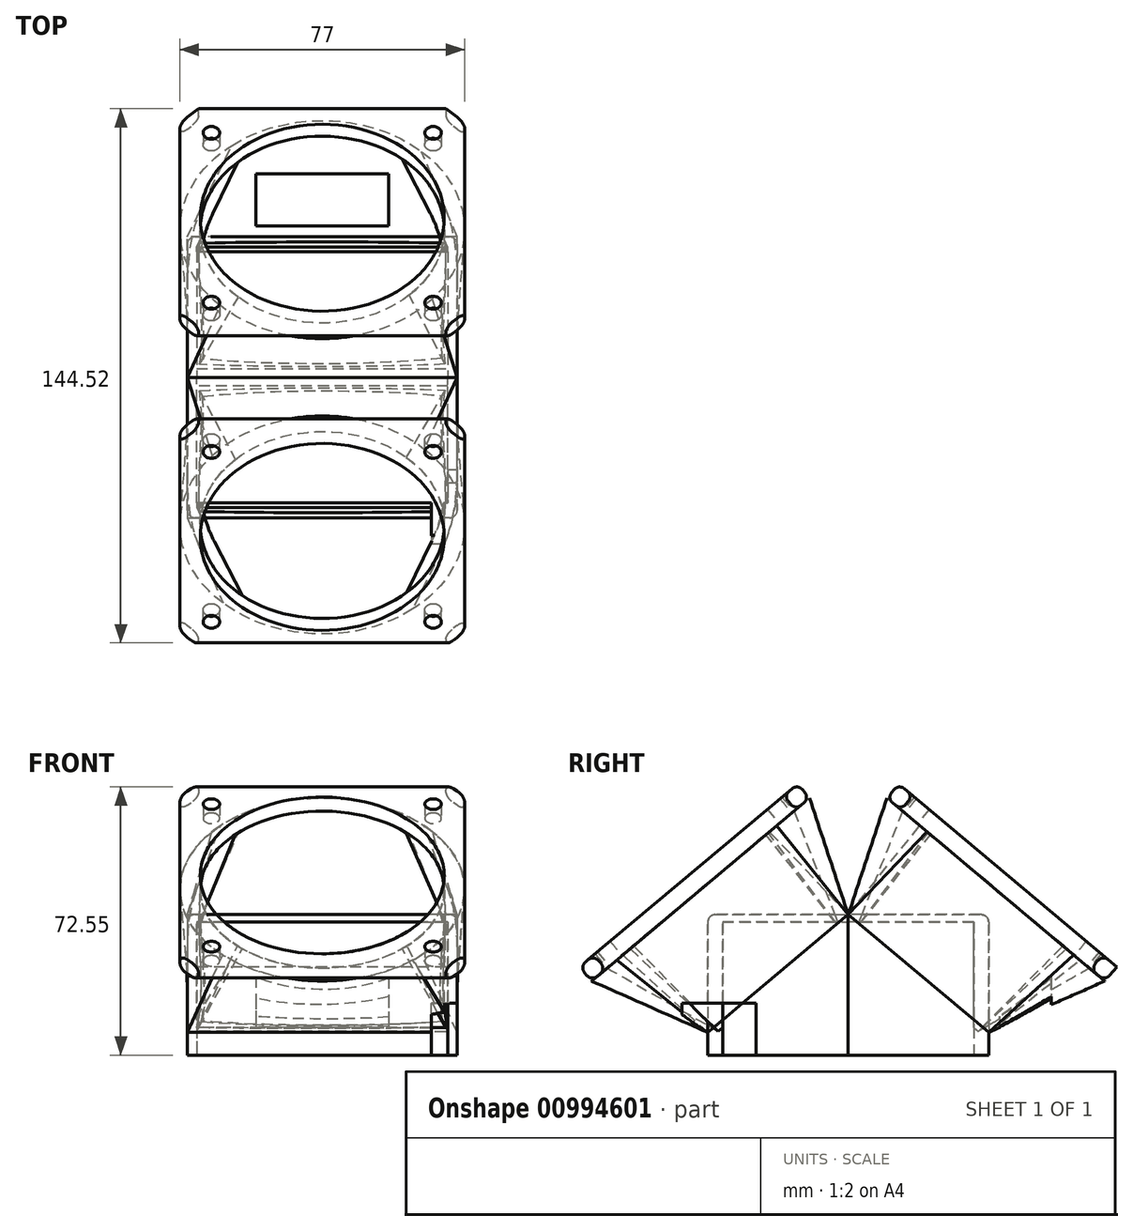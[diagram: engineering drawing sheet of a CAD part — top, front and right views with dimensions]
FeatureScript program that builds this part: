
annotation { "Feature Type Name" : "Feature", "Feature Type Description" : "" }
export const myFeature = defineFeature(function(context is Context, id is Id, definition is map)
    precondition{}
    {
        {
            var Q0;
            Q0=qCreatedBy(makeId("Front.planeOp"),FACE);
            var sketch = newSketch(context, id + "F0", { "sketchPlane" : qUnion([Q0])});
            skLineSegment(sketch, "E0.bottom", {"start": v(-34, 18) * mm, "end": v(34, 18) * mm});
            skLineSegment(sketch, "E0.top", {"start": v(-34, -18) * mm, "end": v(34, -18) * mm});
            skLineSegment(sketch, "E0.left", {"start": v(-34, 18) * mm, "end": v(-34, -18) * mm});
            skLineSegment(sketch, "E0.right", {"start": v(34, 18) * mm, "end": v(34, -18) * mm});
            skPoint(sketch, "E0.middle", {"position": v(0, 0) * mm});
            skSolve(sketch);
        }
        {
            var Q0;
            Q0=makeQuery(id+"F0.imprint","IMPRINT",FACE,{"disambiguationData":[TD([[makeQuery(id+"F0.imprint","IMPRINT",EDGE,{"derivedFrom":sQuery(id+"F0.wireOp",EDGE,"E0.bottom")}),-1.0]])]});
            extrude(context, id + "F1", {"entities" : qUnion([Q0]), "depth" : 34 * mm, "offsetDistance" : 25 * mm});
        }
        {
            var Q0;
            Q0=makeQuery(id+"F0.imprint","IMPRINT",FACE,{"disambiguationData":[TD([[makeQuery(id+"F0.imprint","IMPRINT",EDGE,{"derivedFrom":sQuery(id+"F0.wireOp",EDGE,"E0.bottom")}),-1.0]])]});
            var sketch = newSketch(context, id + "F2", { "sketchPlane" : qUnion([Q0])});
            skLineSegment(sketch, "E1", {"start": v(0, 18) * mm, "end": v(0, -18) * mm, "construction": true});
            skSolve(sketch);
        }
        {
            var Q0;
            Q0=sQuery(id+"F0.wireOp",EDGE,"E0.top");
            cPlane(context, id + "F3", {"entities" : qUnion([Q0]), "cplaneType" : CPlaneType.LINE_ANGLE, "offset" : 25 * mm, "angle" : 50 * degree, "oppositeDirection" : true, "width" : 150 * mm, "height" : 150 * mm});
        }
        {
            var Q0;
            Q0=sQuery(id+"F0.wireOp",EDGE,"E0.bottom");
            var Q1;
            Q1=qBodyType(qCreatedBy(id+"F5",EDGE),BodyType.WIRE);
            cPlane(context, id + "F4", {"entities" : qUnion([Q0, Q1]), "cplaneType" : CPlaneType.LINE_ANGLE, "offset" : 25 * mm, "angle" : 50 * degree, "oppositeDirection" : true, "width" : 150 * mm, "height" : 150 * mm});
        }
        {
            var Q0;
            Q0=qCreatedBy(id+"F4.planeOp",FACE);
            var sketch = newSketch(context, id + "F5", { "sketchPlane" : qUnion([Q0])});
            skLineSegment(sketch, "E2.bottom", {"start": v(34, -8.77) * mm, "end": v(-34, -8.77) * mm});
            skLineSegment(sketch, "E2.top", {"start": v(34, 34.4) * mm, "end": v(-34, 34.4) * mm});
            skLineSegment(sketch, "E2.left", {"start": v(34, -8.77) * mm, "end": v(34, 34.4) * mm});
            skLineSegment(sketch, "E2.right", {"start": v(-34, -8.77) * mm, "end": v(-34, 34.4) * mm});
            skSolve(sketch);
        }
        {
            var Q0;
            Q0=qCreatedBy(id+"F3.planeOp",FACE);
            cPlane(context, id + "F6", {"entities" : qUnion([Q0]), "cplaneType" : CPlaneType.OFFSET, "offset" : 60 * mm, "oppositeDirection" : true, "width" : 150 * mm, "height" : 150 * mm});
        }
        {
            var Q0;
            Q0=qCreatedBy(id+"F6.planeOp",FACE);
            var sketch = newSketch(context, id + "F7", { "sketchPlane" : qUnion([Q0])});
            skArc(sketch, "E3", {"start": v(22.98, 37.08) * mm, "mid": v(0.9, 46.38) * mm, "end": v(-21.64, 38.3) * mm});
            skArc(sketch, "E4", {"start": v(-21.64, 38.3) * mm, "mid": v(-32.97, 14.69) * mm, "end": v(-23.53, -9.74) * mm});
            skArc(sketch, "E5", {"start": v(-23.53, -9.74) * mm, "mid": v(-0.57, -19.6) * mm, "end": v(22.72, -10.54) * mm});
            skArc(sketch, "E6", {"start": v(22.72, -10.54) * mm, "mid": v(33, 13.22) * mm, "end": v(22.98, 37.08) * mm});
            skSolve(sketch);
        }
        {
            var Q0;
            Q0=qSketchRegion(id+"F5",true);
            var Q1;
            Q1=makeQuery(id+"F7.imprint","IMPRINT",FACE,{"disambiguationData":[TD([[makeQuery(id+"F7.imprint","IMPRINT",EDGE,{"derivedFrom":sQuery(id+"F7.wireOp",EDGE,"E3")}),1.0]])]});
            loft(context, id + "F8", {"sheetProfilesArray" : [{ "sheetProfileEntities" : qUnion([Q0]) }, { "sheetProfileEntities" : qUnion([Q1]) }]});
        }
        {
            var Q0;
            Q0=makeQuery(id+"F2.imprint","IMPRINT",FACE,{"disambiguationData":[TD([[makeQuery(id+"F2.imprint","IMPRINT",EDGE,{"derivedFrom":makeQuery(id+"F0.imprint","IMPRINT",EDGE,{"derivedFrom":sQuery(id+"F0.wireOp",EDGE,"E0.bottom")})}),-1.0]])]});
            var sketch = newSketch(context, id + "F9", { "sketchPlane" : qUnion([Q0])});
            skLineSegment(sketch, "E7.bottom", {"start": v(36.5, 20) * mm, "end": v(-36.5, 20) * mm});
            skLineSegment(sketch, "E7.top", {"start": v(36.5, -18) * mm, "end": v(-36.5, -18) * mm});
            skLineSegment(sketch, "E7.left", {"start": v(36.5, 20) * mm, "end": v(36.5, -18) * mm});
            skLineSegment(sketch, "E7.right", {"start": v(-36.5, 20) * mm, "end": v(-36.5, -18) * mm});
            skPoint(sketch, "E7.middle", {"position": v(0, 0) * mm});
            skSolve(sketch);
        }
        {
            var Q0;
            Q0=qSketchRegion(id+"F9",true);
            extrude(context, id + "F10", {"entities" : qUnion([Q0]), "depth" : 38 * mm, "offsetDistance" : 25 * mm});
        }
        {
            var Q0;
            Q0=sQuery(id+"F9.wireOp",EDGE,"E7.bottom");
            cPlane(context, id + "F11", {"entities" : qUnion([Q0]), "cplaneType" : CPlaneType.LINE_ANGLE, "offset" : 25 * mm, "angle" : 50 * degree, "width" : 150 * mm, "height" : 150 * mm});
        }
        {
            var Q0;
            Q0=qCreatedBy(id+"F11.planeOp",FACE);
            var sketch = newSketch(context, id + "F12", { "sketchPlane" : qUnion([Q0])});
            skLineSegment(sketch, "E8.bottom", {"start": v(-36.5, 12.86) * mm, "end": v(36.5, 12.86) * mm});
            skLineSegment(sketch, "E8.top", {"start": v(-36.5, -36.75) * mm, "end": v(36.5, -36.75) * mm});
            skLineSegment(sketch, "E8.left", {"start": v(-36.5, 12.86) * mm, "end": v(-36.5, -36.75) * mm});
            skLineSegment(sketch, "E8.right", {"start": v(36.5, 12.86) * mm, "end": v(36.5, -36.75) * mm});
            skSolve(sketch);
        }
        {
            var Q0;
            Q0=qCreatedBy(id+"F6.planeOp",FACE);
            var sketch = newSketch(context, id + "F13", { "sketchPlane" : qUnion([Q0])});
            skArc(sketch, "E9", {"start": v(-29.82, -10.96) * mm, "mid": v(-1.7, -25.07) * mm, "end": v(27.55, -13.5) * mm});
            skArc(sketch, "E10", {"start": v(27.55, -13.5) * mm, "mid": v(38.44, 15.46) * mm, "end": v(24.51, 43.08) * mm});
            skArc(sketch, "E11", {"start": v(24.51, 43.08) * mm, "mid": v(-1.62, 51.86) * mm, "end": v(-26.92, 40.91) * mm});
            skArc(sketch, "E12", {"start": v(-26.92, 40.91) * mm, "mid": v(-38.44, 15.54) * mm, "end": v(-29.82, -10.96) * mm});
            skSolve(sketch);
        }
        {
            var Q0;
            Q0=qCreatedBy(id+"F6.planeOp",FACE);
            var sketch = newSketch(context, id + "F14", { "sketchPlane" : qUnion([Q0])});
            skLineSegment(sketch, "E13.bottom", {"start": v(-38.5, -25.1) * mm, "end": v(38.5, -25.1) * mm});
            skLineSegment(sketch, "E13.top", {"start": v(-38.5, 51.9) * mm, "end": v(38.5, 51.9) * mm});
            skLineSegment(sketch, "E13.left", {"start": v(-38.5, -25.1) * mm, "end": v(-38.5, 51.9) * mm});
            skLineSegment(sketch, "E13.right", {"start": v(38.5, -25.1) * mm, "end": v(38.5, 51.9) * mm});
            skPoint(sketch, "E13.middle", {"position": v(0, 13.4) * mm});
            skSolve(sketch);
        }
        {
            var Q0;
            Q0=qCreatedBy(id+"F6.planeOp",FACE);
            var sketch = newSketch(context, id + "F15", { "sketchPlane" : qUnion([Q0])});
            skLineSegment(sketch, "E14.bottom", {"start": v(-30, -16.6) * mm, "end": v(30, -16.6) * mm, "construction": true});
            skLineSegment(sketch, "E14.top", {"start": v(-30, 43.4) * mm, "end": v(30, 43.4) * mm, "construction": true});
            skLineSegment(sketch, "E14.left", {"start": v(-30, -16.6) * mm, "end": v(-30, 43.4) * mm, "construction": true});
            skLineSegment(sketch, "E14.right", {"start": v(30, -16.6) * mm, "end": v(30, 43.4) * mm, "construction": true});
            skPoint(sketch, "E14.middle", {"position": v(0, 13.4) * mm});
            skSolve(sketch);
        }
        {
            var Q0;
            Q0=qCreatedBy(id+"F6.planeOp",FACE);
            var sketch = newSketch(context, id + "F16", { "sketchPlane" : qUnion([Q0])});
            skCircle(sketch, "E15", {"center": v(30, -16.6) * mm, "radius": 2.25 * mm});
            skCircle(sketch, "E16", {"center": v(-30, -16.6) * mm, "radius": 2.25 * mm});
            skCircle(sketch, "E17", {"center": v(-30, 43.4) * mm, "radius": 2.25 * mm});
            skCircle(sketch, "E18", {"center": v(30, 43.4) * mm, "radius": 2.25 * mm});
            skSolve(sketch);
        }
        {
            var Q0;
            Q0=makeQuery(id+"F8.opLoft","CAP_FACE",FACE,{"disambiguationData":[OSD([makeQuery(id+"F7.imprint","IMPRINT",FACE,{"disambiguationData":[TD([[makeQuery(id+"F7.imprint","IMPRINT",EDGE,{"derivedFrom":sQuery(id+"F7.wireOp",EDGE,"E3")}),1.0]])]})])],"isStart":true});
            var Q1;
            Q1=makeQuery(id+"F16.imprint","IMPRINT",FACE,{"disambiguationData":[TD([[makeQuery(id+"F16.imprint","IMPRINT",EDGE,{"derivedFrom":sQuery(id+"F16.wireOp",EDGE,"E18")}),1.0]])]});
            var Q2;
            Q2=makeQuery(id+"F16.imprint","IMPRINT",FACE,{"disambiguationData":[TD([[makeQuery(id+"F16.imprint","IMPRINT",EDGE,{"derivedFrom":sQuery(id+"F16.wireOp",EDGE,"E17")}),1.0]])]});
            var Q3;
            Q3=makeQuery(id+"F16.imprint","IMPRINT",FACE,{"disambiguationData":[TD([[makeQuery(id+"F16.imprint","IMPRINT",EDGE,{"derivedFrom":sQuery(id+"F16.wireOp",EDGE,"E16")}),1.0]])]});
            var Q4;
            Q4=makeQuery(id+"F16.imprint","IMPRINT",FACE,{"disambiguationData":[TD([[makeQuery(id+"F16.imprint","IMPRINT",EDGE,{"derivedFrom":sQuery(id+"F16.wireOp",EDGE,"E15")}),1.0]])]});
            extrude(context, id + "F17", {"entities" : qUnion([Q0, Q1, Q2, Q3, Q4]), "depth" : 5 * mm, "offsetDistance" : 25 * mm});
        }
        {
            var Q0;
            Q0=makeQuery(id+"F12.imprint","IMPRINT",FACE,{"disambiguationData":[TD([[makeQuery(id+"F12.imprint","IMPRINT",EDGE,{"derivedFrom":sQuery(id+"F12.wireOp",EDGE,"E8.bottom")}),-1.0]])]});
            var Q1;
            Q1=qSketchRegion(id+"F13",true);
            loft(context, id + "F18", {"sheetProfilesArray" : [{ "sheetProfileEntities" : qUnion([Q0]) }, { "sheetProfileEntities" : qUnion([Q1]) }]});
        }
        {
            var Q0;
            Q0=makeQuery(id+"F14.imprint","IMPRINT",FACE,{"disambiguationData":[TD([[makeQuery(id+"F14.imprint","IMPRINT",EDGE,{"derivedFrom":sQuery(id+"F14.wireOp",EDGE,"E13.bottom")}),1.0]])]});
            extrude(context, id + "F19", {"entities" : qUnion([Q0]), "oppositeDirection" : true, "depth" : 5 * mm, "offsetDistance" : 25 * mm});
        }
        {
            var Q0;
            Q0=makeQuery(id+"F17.opExtrude","SWEPT_BODY",BODY,{"disambiguationData":[OSD([sQuery(id+"F16.wireOp",EDGE,"E18")])]});
            var Q1;
            Q1=makeQuery(id+"F17.opExtrude","SWEPT_BODY",BODY,{"disambiguationData":[OSD([sQuery(id+"F16.wireOp",EDGE,"E17")])]});
            var Q2;
            Q2=makeQuery(id+"F17.opExtrude","SWEPT_BODY",BODY,{"disambiguationData":[OSD([sQuery(id+"F16.wireOp",EDGE,"E16")])]});
            var Q3;
            Q3=makeQuery(id+"F17.opExtrude","SWEPT_BODY",BODY,{"disambiguationData":[OSD([sQuery(id+"F16.wireOp",EDGE,"E15")])]});
            var Q4;
            Q4=makeQuery(id+"F17.opExtrude","SWEPT_BODY",BODY,{"disambiguationData":[OSD([makeQuery(id+"F7.imprint","IMPRINT",FACE,{"disambiguationData":[TD([[makeQuery(id+"F7.imprint","IMPRINT",EDGE,{"derivedFrom":sQuery(id+"F7.wireOp",EDGE,"E3")}),1.0]])]})])]});
            var Q5;
            Q5=makeQuery(id+"F8.opLoft","SWEPT_BODY",BODY,{"disambiguationData":[OSD([makeQuery(id+"F5.imprint","IMPRINT",FACE,{"disambiguationData":[TD([[makeQuery(id+"F5.imprint","IMPRINT",EDGE,{"derivedFrom":sQuery(id+"F5.wireOp",EDGE,"sHmJ6Bm4-Lffu-TfJG-ELbj-xKBSEGzgKOYK.bottom")}),-1.0]])]}),makeQuery(id+"F7.imprint","IMPRINT",FACE,{"disambiguationData":[TD([[makeQuery(id+"F7.imprint","IMPRINT",EDGE,{"derivedFrom":sQuery(id+"F7.wireOp",EDGE,"E3")}),1.0]])]})])]});
            var Q6;
            Q6=makeQuery(id+"F1.opExtrude","SWEPT_BODY",BODY,{"disambiguationData":[OSD([sQuery(id+"F0.wireOp",EDGE,"E0.bottom"),sQuery(id+"F0.wireOp",EDGE,"E0.top"),sQuery(id+"F0.wireOp",EDGE,"E0.left"),sQuery(id+"F0.wireOp",EDGE,"E0.right")])]});
            var Q7;
            Q7=makeQuery(id+"F10.opExtrude","SWEPT_BODY",BODY,{"disambiguationData":[OSD([sQuery(id+"F9.wireOp",EDGE,"E7.bottom"),sQuery(id+"F9.wireOp",EDGE,"E7.top"),sQuery(id+"F9.wireOp",EDGE,"E7.left"),sQuery(id+"F9.wireOp",EDGE,"E7.right")])]});
            var Q8;
            Q8=makeQuery(id+"F18.opLoft","SWEPT_BODY",BODY,{"disambiguationData":[OSD([makeQuery(id+"F12.imprint","IMPRINT",FACE,{"disambiguationData":[TD([[makeQuery(id+"F12.imprint","IMPRINT",EDGE,{"derivedFrom":sQuery(id+"F12.wireOp",EDGE,"E8.bottom")}),-1.0]])]}),makeQuery(id+"F13.imprint","IMPRINT",FACE,{"disambiguationData":[TD([[makeQuery(id+"F13.imprint","IMPRINT",EDGE,{"derivedFrom":sQuery(id+"F13.wireOp",EDGE,"q23MTACi-eoCC-Vc5T-UU1i-hVDggLDGJppy")}),1.0]])]})])]});
            var Q9;
            Q9=makeQuery(id+"F19.opExtrude","SWEPT_BODY",BODY,{"disambiguationData":[OSD([sQuery(id+"F14.wireOp",EDGE,"E13.bottom"),sQuery(id+"F14.wireOp",EDGE,"E13.top"),sQuery(id+"F14.wireOp",EDGE,"E13.left"),sQuery(id+"F14.wireOp",EDGE,"E13.right")])]});
            booleanBodies(context, id + "F20", {"operationType" : BooleanOperationType.SUBTRACTION, "tools" : qUnion([Q0, Q1, Q2, Q3, Q4, Q5, Q6]), "targets" : qUnion([Q7, Q8, Q9])});
        }
        {
            var Q0;
            Q0=makeQuery(id+"F10.opExtrude","SWEPT_BODY",BODY,{"disambiguationData":[OSD([sQuery(id+"F9.wireOp",EDGE,"E7.bottom"),sQuery(id+"F9.wireOp",EDGE,"E7.top"),sQuery(id+"F9.wireOp",EDGE,"E7.left"),sQuery(id+"F9.wireOp",EDGE,"E7.right")])]});
            var Q1;
            Q1=sQuery(id+"F2.wireOp",EDGE,"E1");
            transform(context, id + "F21", {"entities" : qUnion([Q0]), "transformType" : TransformType.ROTATION, "transformAxis" : qUnion([Q1]), "angle" : 180 * degree, "makeCopy" : true});
        }
        {
            var Q0;
            Q0=makeQuery(id+"F18.opLoft","SWEPT_BODY",BODY,{"disambiguationData":[OSD([makeQuery(id+"F12.imprint","IMPRINT",FACE,{"disambiguationData":[TD([[makeQuery(id+"F12.imprint","IMPRINT",EDGE,{"derivedFrom":sQuery(id+"F12.wireOp",EDGE,"E8.bottom")}),-1.0]])]}),makeQuery(id+"F13.imprint","IMPRINT",FACE,{"disambiguationData":[TD([[makeQuery(id+"F13.imprint","IMPRINT",EDGE,{"derivedFrom":sQuery(id+"F13.wireOp",EDGE,"q23MTACi-eoCC-Vc5T-UU1i-hVDggLDGJppy")}),1.0]])]})])]});
            var Q1;
            Q1=sQuery(id+"F2.wireOp",EDGE,"E1");
            transform(context, id + "F22", {"entities" : qUnion([Q0]), "transformType" : TransformType.ROTATION, "transformAxis" : qUnion([Q1]), "angle" : 180 * degree, "makeCopy" : true});
        }
        {
            var Q0;
            Q0=makeQuery(id+"F19.opExtrude","SWEPT_BODY",BODY,{"disambiguationData":[OSD([sQuery(id+"F14.wireOp",EDGE,"E13.bottom"),sQuery(id+"F14.wireOp",EDGE,"E13.top"),sQuery(id+"F14.wireOp",EDGE,"E13.left"),sQuery(id+"F14.wireOp",EDGE,"E13.right")])]});
            var Q1;
            Q1=sQuery(id+"F2.wireOp",EDGE,"E1");
            transform(context, id + "F23", {"entities" : qUnion([Q0]), "transformType" : TransformType.ROTATION, "transformAxis" : qUnion([Q1]), "angle" : 180 * degree, "makeCopy" : true});
        }
        {
            var Q0;
            Q0=makeQuery(id+"F19.opExtrude","SWEPT_EDGE",EDGE,{"disambiguationData":[OSD([sQuery(id+"F14.wireOp",EDGE,"E13.top"),sQuery(id+"F14.wireOp",EDGE,"E13.right")])]});
            var Q1;
            Q1=makeQuery(id+"F19.opExtrude","SWEPT_EDGE",EDGE,{"disambiguationData":[OSD([sQuery(id+"F14.wireOp",EDGE,"E13.top"),sQuery(id+"F14.wireOp",EDGE,"E13.left")])]});
            var Q2;
            Q2=makeQuery(id+"F19.opExtrude","SWEPT_EDGE",EDGE,{"disambiguationData":[OSD([sQuery(id+"F14.wireOp",EDGE,"E13.bottom"),sQuery(id+"F14.wireOp",EDGE,"E13.right")])]});
            var Q3;
            Q3=makeQuery(id+"F19.opExtrude","SWEPT_EDGE",EDGE,{"disambiguationData":[OSD([sQuery(id+"F14.wireOp",EDGE,"E13.bottom"),sQuery(id+"F14.wireOp",EDGE,"E13.left")])]});
            var Q4;
            Q4=makeQuery(id+"F23.opPattern","COPY",EDGE,{"derivedFrom":makeQuery(id+"F19.opExtrude","SWEPT_EDGE",EDGE,{"disambiguationData":[OSD([sQuery(id+"F14.wireOp",EDGE,"E13.bottom"),sQuery(id+"F14.wireOp",EDGE,"E13.right")])]}),"instanceName":"1"});
            var Q5;
            Q5=makeQuery(id+"F23.opPattern","COPY",EDGE,{"derivedFrom":makeQuery(id+"F19.opExtrude","SWEPT_EDGE",EDGE,{"disambiguationData":[OSD([sQuery(id+"F14.wireOp",EDGE,"E13.bottom"),sQuery(id+"F14.wireOp",EDGE,"E13.left")])]}),"instanceName":"1"});
            var Q6;
            Q6=makeQuery(id+"F23.opPattern","COPY",EDGE,{"derivedFrom":makeQuery(id+"F19.opExtrude","SWEPT_EDGE",EDGE,{"disambiguationData":[OSD([sQuery(id+"F14.wireOp",EDGE,"E13.top"),sQuery(id+"F14.wireOp",EDGE,"E13.left")])]}),"instanceName":"1"});
            var Q7;
            Q7=makeQuery(id+"F23.opPattern","COPY",EDGE,{"derivedFrom":makeQuery(id+"F19.opExtrude","SWEPT_EDGE",EDGE,{"disambiguationData":[OSD([sQuery(id+"F14.wireOp",EDGE,"E13.top"),sQuery(id+"F14.wireOp",EDGE,"E13.right")])]}),"instanceName":"1"});
            chamfer(context, id + "F24", {"entities" : qUnion([Q0, Q1, Q2, Q3, Q4, Q5, Q6, Q7]), "width" : 5 * mm, "tangentPropagation" : true});
        }
        {
            var Q0;
            Q0=makeQuery(id+"F19.opExtrude","CAP_EDGE",EDGE,{"disambiguationData":[OSD([sQuery(id+"F14.wireOp",EDGE,"E13.left")])],"isStart":false});
            var Q1;
            Q1=makeQuery(id+"F19.opExtrude","CAP_EDGE",EDGE,{"disambiguationData":[OSD([sQuery(id+"F14.wireOp",EDGE,"E13.top")])],"isStart":false});
            var Q2;
            Q2=makeQuery(id+"F19.opExtrude","CAP_EDGE",EDGE,{"disambiguationData":[OSD([sQuery(id+"F14.wireOp",EDGE,"E13.right")])],"isStart":false});
            var Q3;
            Q3=makeQuery(id+"F19.opExtrude","CAP_EDGE",EDGE,{"disambiguationData":[OSD([sQuery(id+"F14.wireOp",EDGE,"E13.bottom")])],"isStart":false});
            var Q4;
            Q4=makeQuery(id+"F19.opExtrude","CAP_EDGE",EDGE,{"disambiguationData":[OSD([sQuery(id+"F14.wireOp",EDGE,"E13.left")])],"isStart":true});
            var Q5;
            Q5=makeQuery(id+"F19.opExtrude","CAP_EDGE",EDGE,{"disambiguationData":[OSD([sQuery(id+"F14.wireOp",EDGE,"E13.bottom")])],"isStart":true});
            var Q6;
            Q6=makeQuery(id+"F19.opExtrude","CAP_EDGE",EDGE,{"disambiguationData":[OSD([sQuery(id+"F14.wireOp",EDGE,"E13.right")])],"isStart":true});
            var Q7;
            Q7=makeQuery(id+"F19.opExtrude","CAP_EDGE",EDGE,{"disambiguationData":[OSD([sQuery(id+"F14.wireOp",EDGE,"E13.top")])],"isStart":true});
            var Q8;
            Q8=makeQuery(id+"F10.opExtrude","CAP_EDGE",EDGE,{"disambiguationData":[OSD([sQuery(id+"F9.wireOp",EDGE,"E7.right")])],"isStart":false});
            var Q9;
            {var subQ0=sQuery(id+"F9.wireOp",EDGE,"E7.bottom");var subQ1=sQuery(id+"F9.wireOp",EDGE,"E7.right");Q9=makeQuery(id+"F20.opBoolean","SPLIT",EDGE,{"disambiguationData":[TD([makeQuery(id+"F10.opExtrude","SWEPT_FACE",FACE,{"disambiguationData":[OSD([subQ1])]})])],"derivedFrom":makeQuery(id+"F10.opExtrude","CAP_EDGE",EDGE,{"disambiguationData":[OSD([subQ0])],"isStart":false})});}
            var Q10;
            Q10=makeQuery(id+"F10.opExtrude","SWEPT_EDGE",EDGE,{"disambiguationData":[OSD([sQuery(id+"F9.wireOp",EDGE,"E7.bottom"),sQuery(id+"F9.wireOp",EDGE,"E7.right")])]});
            var Q11;
            Q11=makeQuery(id+"F10.opExtrude","CAP_EDGE",EDGE,{"disambiguationData":[OSD([sQuery(id+"F9.wireOp",EDGE,"E7.left")])],"isStart":false});
            var Q12;
            Q12=makeQuery(id+"F10.opExtrude","SWEPT_EDGE",EDGE,{"disambiguationData":[OSD([sQuery(id+"F9.wireOp",EDGE,"E7.bottom"),sQuery(id+"F9.wireOp",EDGE,"E7.left")])]});
            var Q13;
            {var subQ0=sQuery(id+"F9.wireOp",EDGE,"E7.bottom");var subQ1=sQuery(id+"F9.wireOp",EDGE,"E7.left");Q13=makeQuery(id+"F20.opBoolean","SPLIT",EDGE,{"disambiguationData":[TD([makeQuery(id+"F10.opExtrude","SWEPT_FACE",FACE,{"disambiguationData":[OSD([subQ1])]})])],"derivedFrom":makeQuery(id+"F10.opExtrude","CAP_EDGE",EDGE,{"disambiguationData":[OSD([subQ0])],"isStart":false})});}
            var Q14;
            Q14=makeQuery(id+"F21.opPattern","COPY",EDGE,{"derivedFrom":makeQuery(id+"F10.opExtrude","SWEPT_EDGE",EDGE,{"disambiguationData":[OSD([sQuery(id+"F9.wireOp",EDGE,"E7.bottom"),sQuery(id+"F9.wireOp",EDGE,"E7.right")])]}),"instanceName":"1"});
            var Q15;
            {var subQ0=sQuery(id+"F9.wireOp",EDGE,"E7.bottom");var subQ1=sQuery(id+"F9.wireOp",EDGE,"E7.right");Q15=makeQuery(id+"F21.opPattern","COPY",EDGE,{"derivedFrom":makeQuery(id+"F20.opBoolean","SPLIT",EDGE,{"disambiguationData":[TD([makeQuery(id+"F10.opExtrude","SWEPT_FACE",FACE,{"disambiguationData":[OSD([subQ1])]})])],"derivedFrom":makeQuery(id+"F10.opExtrude","CAP_EDGE",EDGE,{"disambiguationData":[OSD([subQ0])],"isStart":false})}),"instanceName":"1"});}
            var Q16;
            Q16=makeQuery(id+"F21.opPattern","COPY",EDGE,{"derivedFrom":makeQuery(id+"F10.opExtrude","CAP_EDGE",EDGE,{"disambiguationData":[OSD([sQuery(id+"F9.wireOp",EDGE,"E7.right")])],"isStart":false}),"instanceName":"1"});
            var Q17;
            Q17=makeQuery(id+"F23.opPattern","COPY",EDGE,{"derivedFrom":makeQuery(id+"F19.opExtrude","CAP_EDGE",EDGE,{"disambiguationData":[OSD([sQuery(id+"F14.wireOp",EDGE,"E13.right")])],"isStart":false}),"instanceName":"1"});
            var Q18;
            Q18=makeQuery(id+"F23.opPattern","COPY",EDGE,{"derivedFrom":makeQuery(id+"F19.opExtrude","CAP_EDGE",EDGE,{"disambiguationData":[OSD([sQuery(id+"F14.wireOp",EDGE,"E13.right")])],"isStart":true}),"instanceName":"1"});
            var Q19;
            Q19=makeQuery(id+"F23.opPattern","COPY",EDGE,{"derivedFrom":makeQuery(id+"F19.opExtrude","CAP_EDGE",EDGE,{"disambiguationData":[OSD([sQuery(id+"F14.wireOp",EDGE,"E13.top")])],"isStart":true}),"instanceName":"1"});
            var Q20;
            Q20=makeQuery(id+"F23.opPattern","COPY",EDGE,{"derivedFrom":makeQuery(id+"F19.opExtrude","CAP_EDGE",EDGE,{"disambiguationData":[OSD([sQuery(id+"F14.wireOp",EDGE,"E13.bottom")])],"isStart":true}),"instanceName":"1"});
            var Q21;
            Q21=makeQuery(id+"F23.opPattern","COPY",EDGE,{"derivedFrom":makeQuery(id+"F19.opExtrude","CAP_EDGE",EDGE,{"disambiguationData":[OSD([sQuery(id+"F14.wireOp",EDGE,"E13.bottom")])],"isStart":false}),"instanceName":"1"});
            var Q22;
            Q22=makeQuery(id+"F23.opPattern","COPY",EDGE,{"derivedFrom":makeQuery(id+"F19.opExtrude","CAP_EDGE",EDGE,{"disambiguationData":[OSD([sQuery(id+"F14.wireOp",EDGE,"E13.left")])],"isStart":false}),"instanceName":"1"});
            var Q23;
            Q23=makeQuery(id+"F23.opPattern","COPY",EDGE,{"derivedFrom":makeQuery(id+"F19.opExtrude","CAP_EDGE",EDGE,{"disambiguationData":[OSD([sQuery(id+"F14.wireOp",EDGE,"E13.left")])],"isStart":true}),"instanceName":"1"});
            var Q24;
            Q24=makeQuery(id+"F21.opPattern","COPY",EDGE,{"derivedFrom":makeQuery(id+"F10.opExtrude","CAP_EDGE",EDGE,{"disambiguationData":[OSD([sQuery(id+"F9.wireOp",EDGE,"E7.left")])],"isStart":false}),"instanceName":"1"});
            var Q25;
            {var subQ0=sQuery(id+"F9.wireOp",EDGE,"E7.bottom");var subQ1=sQuery(id+"F9.wireOp",EDGE,"E7.left");Q25=makeQuery(id+"F21.opPattern","COPY",EDGE,{"derivedFrom":makeQuery(id+"F20.opBoolean","SPLIT",EDGE,{"disambiguationData":[TD([makeQuery(id+"F10.opExtrude","SWEPT_FACE",FACE,{"disambiguationData":[OSD([subQ1])]})])],"derivedFrom":makeQuery(id+"F10.opExtrude","CAP_EDGE",EDGE,{"disambiguationData":[OSD([subQ0])],"isStart":false})}),"instanceName":"1"});}
            var Q26;
            Q26=makeQuery(id+"F21.opPattern","COPY",EDGE,{"derivedFrom":makeQuery(id+"F10.opExtrude","SWEPT_EDGE",EDGE,{"disambiguationData":[OSD([sQuery(id+"F9.wireOp",EDGE,"E7.bottom"),sQuery(id+"F9.wireOp",EDGE,"E7.left")])]}),"instanceName":"1"});
            fillet(context, id + "F25", {"entities" : qUnion([Q0, Q1, Q2, Q3, Q4, Q5, Q6, Q7, Q8, Q9, Q10, Q11, Q12, Q13, Q14, Q15, Q16, Q17, Q18, Q19, Q20, Q21, Q22, Q23, Q24, Q25, Q26]), "radius" : 2 * mm, "tangentPropagation" : true, "allowEdgeOverflow" : false});
        }
        {
            var Q0;
            Q0=makeQuery(id+"F10.opExtrude","SWEPT_FACE",FACE,{"disambiguationData":[OSD([sQuery(id+"F9.wireOp",EDGE,"E7.left")])]});
            var sketch = newSketch(context, id + "F26", { "sketchPlane" : qUnion([Q0])});
            skLineSegment(sketch, "E19.bottom", {"start": v(-25, -19) * mm, "end": v(-45, -19) * mm});
            skLineSegment(sketch, "E19.top", {"start": v(-25, -4) * mm, "end": v(-45, -4) * mm});
            skLineSegment(sketch, "E19.left", {"start": v(-25, -19) * mm, "end": v(-25, -4) * mm});
            skLineSegment(sketch, "E19.right", {"start": v(-45, -19) * mm, "end": v(-45, -4) * mm});
            skSolve(sketch);
        }
        {
            var Q0;
            Q0=qSketchRegion(id+"F26",true);
            extrude(context, id + "F27", {"entities" : qUnion([Q0]), "oppositeDirection" : true, "depth" : 7 * mm, "offsetDistance" : 25 * mm});
        }
        {
            var Q0;
            Q0=makeQuery(id+"F27.opExtrude","SWEPT_BODY",BODY,{"disambiguationData":[OSD([sQuery(id+"F26.wireOp",EDGE,"E19.bottom"),sQuery(id+"F26.wireOp",EDGE,"E19.top"),sQuery(id+"F26.wireOp",EDGE,"E19.left"),sQuery(id+"F26.wireOp",EDGE,"E19.right")])]});
            var Q1;
            Q1=makeQuery(id+"F10.opExtrude","SWEPT_BODY",BODY,{"disambiguationData":[OSD([sQuery(id+"F9.wireOp",EDGE,"E7.bottom"),sQuery(id+"F9.wireOp",EDGE,"E7.top"),sQuery(id+"F9.wireOp",EDGE,"E7.left"),sQuery(id+"F9.wireOp",EDGE,"E7.right")])]});
            var Q2;
            Q2=makeQuery(id+"F18.opLoft","SWEPT_BODY",BODY,{"disambiguationData":[OSD([makeQuery(id+"F12.imprint","IMPRINT",FACE,{"disambiguationData":[TD([[makeQuery(id+"F12.imprint","IMPRINT",EDGE,{"derivedFrom":sQuery(id+"F12.wireOp",EDGE,"E8.bottom")}),-1.0]])]}),makeQuery(id+"F13.imprint","IMPRINT",FACE,{"disambiguationData":[TD([[makeQuery(id+"F13.imprint","IMPRINT",EDGE,{"derivedFrom":sQuery(id+"F13.wireOp",EDGE,"q23MTACi-eoCC-Vc5T-UU1i-hVDggLDGJppy")}),1.0]])]})])]});
            booleanBodies(context, id + "F28", {"operationType" : BooleanOperationType.SUBTRACTION, "tools" : qUnion([Q0]), "targets" : qUnion([Q1, Q2])});
        }
        {
            var Q0;
            Q0=qCreatedBy(makeId("Top.planeOp"),FACE);
            var sketch = newSketch(context, id + "F29", { "sketchPlane" : qUnion([Q0])});
            skLineSegment(sketch, "E20.bottom", {"start": v(18, 55) * mm, "end": v(-18, 55) * mm});
            skLineSegment(sketch, "E20.top", {"start": v(18, 41) * mm, "end": v(-18, 41) * mm});
            skLineSegment(sketch, "E20.left", {"start": v(18, 55) * mm, "end": v(18, 41) * mm});
            skLineSegment(sketch, "E20.right", {"start": v(-18, 55) * mm, "end": v(-18, 41) * mm});
            skPoint(sketch, "E20.middle", {"position": v(0, 48) * mm});
            skSolve(sketch);
        }
        {
            var Q0;
            Q0 = qSketchRegion(id + "F29", true);
            extrude(context, id + "F30", {"entities" : qUnion([Q0]), "endBound" : BoundingType.SYMMETRIC, "depth" : 25 * mm, "offsetDistance" : 25 * mm});
        }
        {
            var Q0;
            Q0=makeQuery(id+"F30.opExtrude","SWEPT_BODY",BODY,{"disambiguationData":[OSD([sQuery(id+"F29.wireOp",EDGE,"E20.bottom"),sQuery(id+"F29.wireOp",EDGE,"E20.top"),sQuery(id+"F29.wireOp",EDGE,"E20.left"),sQuery(id+"F29.wireOp",EDGE,"E20.right")])]});
            var Q1;
            Q1=makeQuery(id+"F23.opPattern","COPY",BODY,{"derivedFrom":makeQuery(id+"F19.opExtrude","SWEPT_BODY",BODY,{"disambiguationData":[OSD([sQuery(id+"F14.wireOp",EDGE,"E13.bottom"),sQuery(id+"F14.wireOp",EDGE,"E13.top"),sQuery(id+"F14.wireOp",EDGE,"E13.left"),sQuery(id+"F14.wireOp",EDGE,"E13.right")])]}),"instanceName":"1"});
            var Q2;
            Q2=makeQuery(id+"F22.opPattern","COPY",BODY,{"derivedFrom":makeQuery(id+"F18.opLoft","SWEPT_BODY",BODY,{"disambiguationData":[OSD([makeQuery(id+"F12.imprint","IMPRINT",FACE,{"disambiguationData":[TD([[makeQuery(id+"F12.imprint","IMPRINT",EDGE,{"derivedFrom":sQuery(id+"F12.wireOp",EDGE,"E8.bottom")}),-1.0]])]}),makeQuery(id+"F13.imprint","IMPRINT",FACE,{"disambiguationData":[TD([[makeQuery(id+"F13.imprint","IMPRINT",EDGE,{"derivedFrom":sQuery(id+"F13.wireOp",EDGE,"E9")}),1.0]])]})])]}),"instanceName":"1"});
            var Q3;
            Q3=makeQuery(id+"F21.opPattern","COPY",BODY,{"derivedFrom":makeQuery(id+"F10.opExtrude","SWEPT_BODY",BODY,{"disambiguationData":[OSD([sQuery(id+"F9.wireOp",EDGE,"E7.bottom"),sQuery(id+"F9.wireOp",EDGE,"E7.top"),sQuery(id+"F9.wireOp",EDGE,"E7.left"),sQuery(id+"F9.wireOp",EDGE,"E7.right")])]}),"instanceName":"1"});
            booleanBodies(context, id + "F31", {"operationType" : BooleanOperationType.SUBTRACTION, "tools" : qUnion([Q0]), "targets" : qUnion([Q1, Q2, Q3])});
        }
    });
